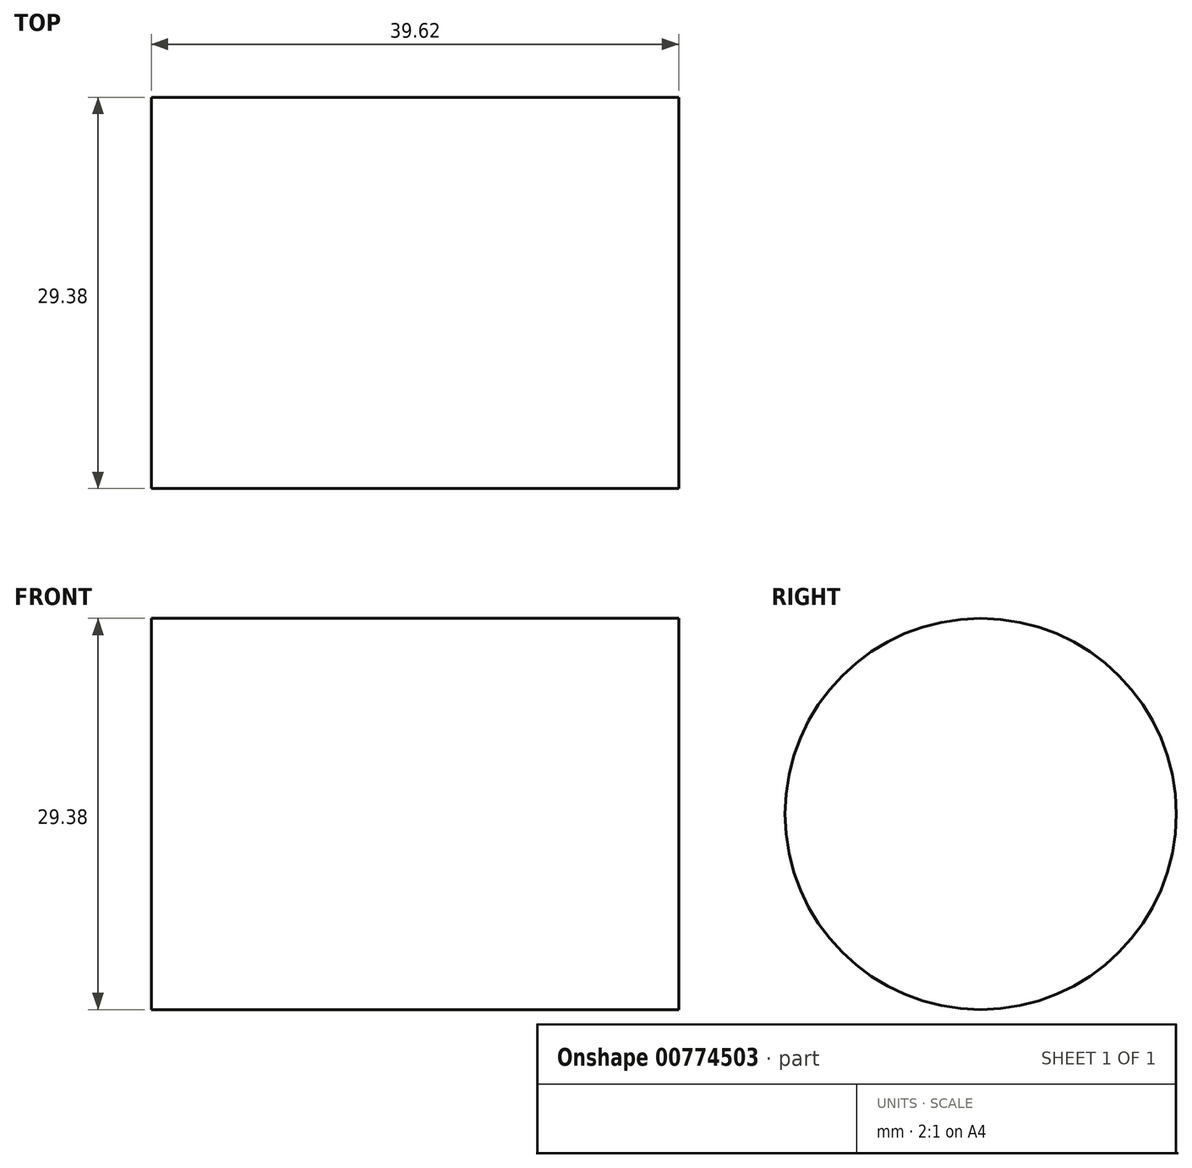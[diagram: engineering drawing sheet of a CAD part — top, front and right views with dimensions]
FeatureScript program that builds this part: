
annotation { "Feature Type Name" : "Feature", "Feature Type Description" : "" }
export const myFeature = defineFeature(function(context is Context, id is Id, definition is map)
    precondition{}
    {
        {
            var Q0;
            Q0=qCreatedBy(makeId("Front.planeOp"),FACE);
            var sketch = newSketch(context, id + "F0", { "sketchPlane" : qUnion([Q0])});
            skLineSegment(sketch, "E0.bottom", {"start": v(0, 0) * mm, "end": v(39.62, 0) * mm});
            skLineSegment(sketch, "E0.top", {"start": v(0, -14.7) * mm, "end": v(39.62, -14.7) * mm});
            skLineSegment(sketch, "E0.left", {"start": v(0, 0) * mm, "end": v(0, -14.7) * mm});
            skLineSegment(sketch, "E0.right", {"start": v(39.62, 0) * mm, "end": v(39.62, -14.7) * mm});
            skSolve(sketch);
        }
        {
            var Q0;
            Q0 = qSketchRegion(id + "F0", true);
            var Q1;
            Q1=sQuery(id+"F0.wireOp",EDGE,"E0.bottom");
            revolve(context, id + "F1", {"surfaceOperationType" : NewSurfaceOperationType.NEW, "entities" : qUnion([Q0]), "axis" : qUnion([Q1]), "revolveType" : RevolveType.FULL});
        }
    });
